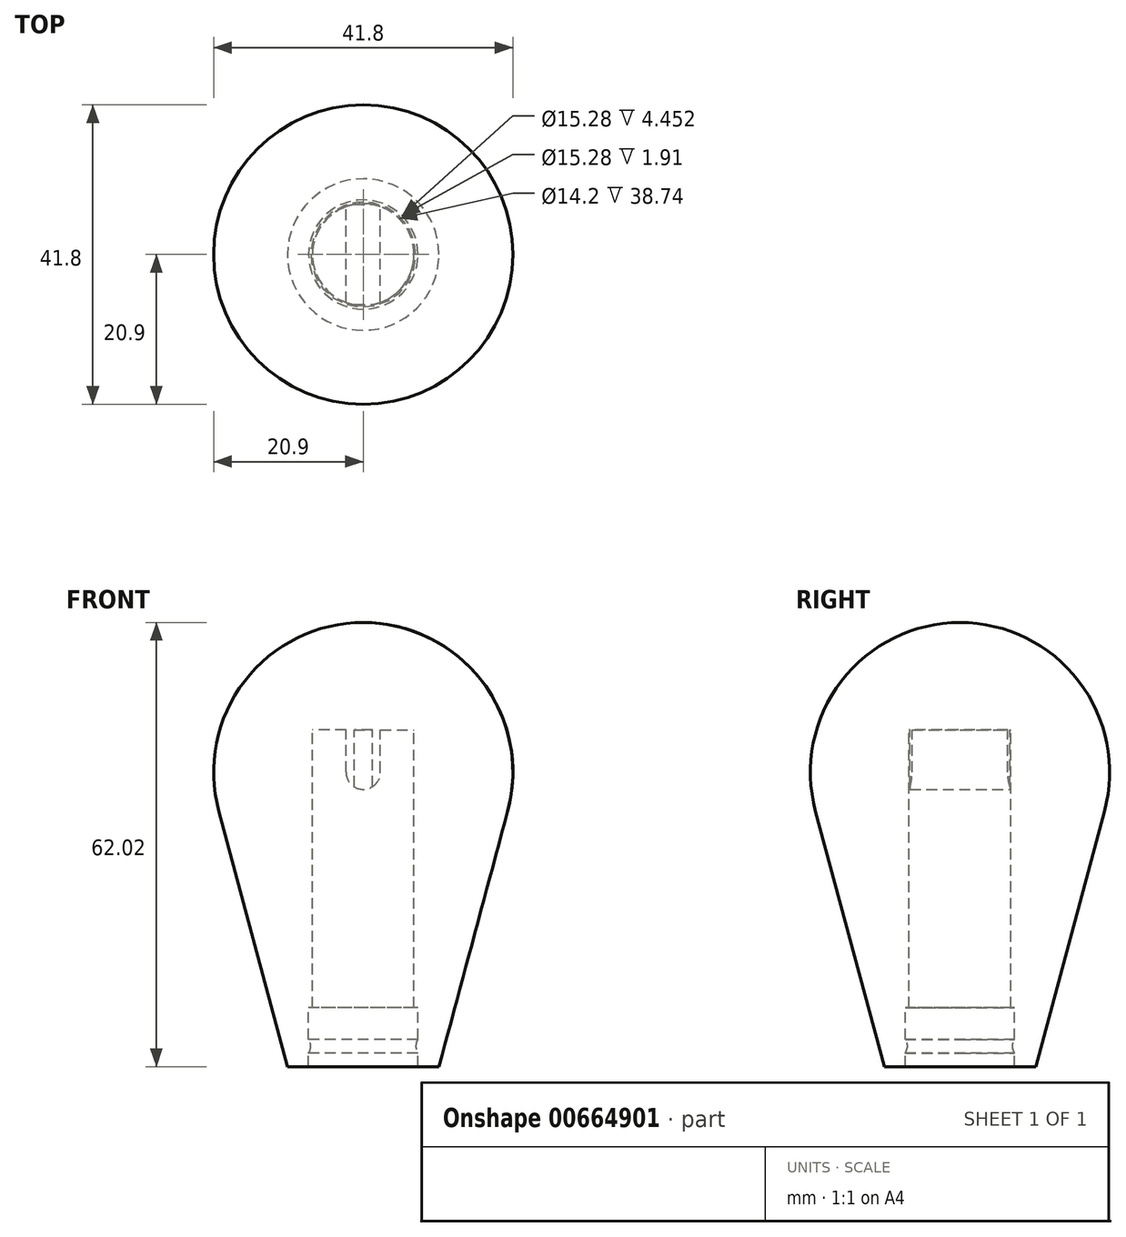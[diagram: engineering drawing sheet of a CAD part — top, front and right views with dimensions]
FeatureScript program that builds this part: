
annotation { "Feature Type Name" : "Feature", "Feature Type Description" : "" }
export const myFeature = defineFeature(function(context is Context, id is Id, definition is map)
    precondition{}
    {
        {
            var Q0;
            Q0=qCreatedBy(makeId("Front.planeOp"),FACE);
            var sketch = newSketch(context, id + "F0", { "sketchPlane" : qUnion([Q0])});
            skLineSegment(sketch, "E0", {"start": v(0, 0) * mm, "end": v(7.1, 0) * mm});
            skLineSegment(sketch, "E1", {"start": v(20.18, -11.3) * mm, "end": v(10.58, -47) * mm});
            skLineSegment(sketch, "E2", {"start": v(7.1, 0) * mm, "end": v(7.1, -38.74) * mm});
            skLineSegment(sketch, "E3", {"start": v(7.64, -47) * mm, "end": v(10.58, -47) * mm});
            skLineSegment(sketch, "E4", {"start": v(7.64, -38.74) * mm, "end": v(7.1, -38.74) * mm});
            skLineSegment(sketch, "E5", {"start": v(0, 0) * mm, "end": v(2.4, 0) * mm});
            skLineSegment(sketch, "E6", {"start": v(2.4, 0) * mm, "end": v(2.4, -5.88) * mm});
            skLineSegment(sketch, "E7", {"start": v(2.4, -5.88) * mm, "end": v(0, -5.88) * mm});
            skLineSegment(sketch, "E8", {"start": v(0, -5.88) * mm, "end": v(-2.4, -5.88) * mm});
            skLineSegment(sketch, "E9", {"start": v(-2.4, -5.88) * mm, "end": v(-2.4, 0) * mm});
            skLineSegment(sketch, "E10", {"start": v(-2.4, 0) * mm, "end": v(0, 0) * mm});
            skArc(sketch, "E11", {"start": v(2.4, -5.88) * mm, "mid": v(0, -8.28) * mm, "end": v(-2.4, -5.88) * mm});
            skLineSegment(sketch, "E12", {"start": v(7.64, -47) * mm, "end": v(7.64, -44.14) * mm});
            skLineSegment(sketch, "E13", {"start": v(7.64, -44.14) * mm, "end": v(7.64, -38.74) * mm});
            skLineSegment(sketch, "E14", {"start": v(7.64, -44.14) * mm, "end": v(7.34, -44.14) * mm});
            skLineSegment(sketch, "E15", {"start": v(7.64, -44.14) * mm, "end": v(7.64, -43.2) * mm});
            skLineSegment(sketch, "E16", {"start": v(7.64, -44.14) * mm, "end": v(7.64, -45.1) * mm});
            skArc(sketch, "E17", {"start": v(7.64, -43.2) * mm, "mid": v(7.34, -44.14) * mm, "end": v(7.64, -45.1) * mm});
            skArc(sketch, "E18", {"start": v(0, 15.02) * mm, "mid": v(16.58, 6.83) * mm, "end": v(20.18, -11.3) * mm});
            skLineSegment(sketch, "E19", {"start": v(0, 15.02) * mm, "end": v(0, 0) * mm});
            skSolve(sketch);
        }
        {
            var Q0;
            {var subQ0=sQuery(id+"F0.wireOp",EDGE,"E6");Q0=makeQuery(id+"F0.imprint","IMPRINT",FACE,{"disambiguationData":[TD([[makeQuery(id+"F0.imprint","IMPRINT",EDGE,{"derivedFrom":subQ0}),-1.0]])]});}
            var Q1;
            Q1=makeQuery(id+"F0.imprint","IMPRINT",FACE,{"disambiguationData":[TD([[makeQuery(id+"F0.imprint","IMPRINT",EDGE,{"derivedFrom":sQuery(id+"F0.wireOp",EDGE,"E7")}),1.0]])]});
            extrude(context, id + "F1", {"entities" : qUnion([Q0, Q1]), "endBound" : BoundingType.SYMMETRIC, "depth" : 13.97 * mm, "offsetDistance" : 25.4 * mm});
        }
        {
            var Q0;
            Q0=makeQuery(id+"F0.imprint","IMPRINT",FACE,{"disambiguationData":[TD([[makeQuery(id+"F0.imprint","IMPRINT",EDGE,{"derivedFrom":sQuery(id+"F0.wireOp",EDGE,"E1")}),-1.0]])]});
            var Q1;
            {var subQ0=sQuery(id+"F0.wireOp",EDGE,"E14");Q1=makeQuery(id+"F0.imprint","IMPRINT",FACE,{"disambiguationData":[TD([[makeQuery(id+"F0.imprint","IMPRINT",EDGE,{"derivedFrom":subQ0}),-1.0]])]});}
            var Q2;
            {var subQ0=sQuery(id+"F0.wireOp",EDGE,"E14");Q2=makeQuery(id+"F0.imprint","IMPRINT",FACE,{"disambiguationData":[TD([[makeQuery(id+"F0.imprint","IMPRINT",EDGE,{"derivedFrom":subQ0}),1.0]])]});}
            var Q3;
            Q3=sQuery(id+"F0.wireOp",EDGE,"E19");
            revolve(context, id + "F2", {"operationType" : NewBodyOperationType.ADD, "surfaceOperationType" : NewSurfaceOperationType.NEW, "entities" : qUnion([Q0, Q1, Q2]), "axis" : qUnion([Q3]), "revolveType" : RevolveType.FULL});
        }
    });
